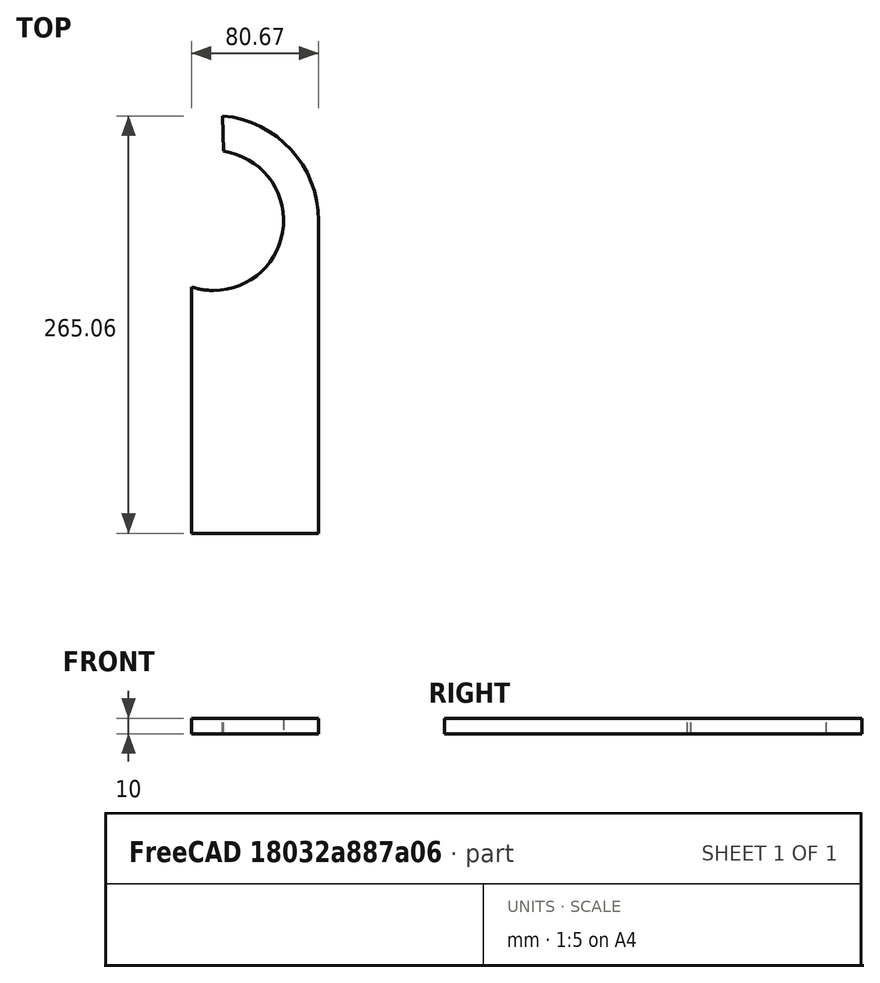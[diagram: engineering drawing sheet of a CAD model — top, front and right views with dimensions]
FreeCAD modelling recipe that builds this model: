
FCSTD DOCUMENT  (FreeCAD 0.21R33675 (Git))
Label: Tail_Stop_LowEnd
License: All rights reserved
LicenseURL: http://en.wikipedia.org/wiki/All_rights_reserved
objects: Sketcher::SketchObject×1, PartDesign::Pad×1, Spreadsheet::Sheet×1, PartDesign::Body×1
note: 4 computed .brp shape members not serialized (recipe doc carries the construction recipe); baked Part::Feature solids carry a one-line shape summary decoded from their .brp
EXTERNAL_REF file=../../Master_of_Puppets.FCStd obj=LowEndStop
EXTERNAL_REF file=../../Master_of_Puppets.FCStd obj=Spreadsheet
EXTERNAL_REF file=../../Master_of_Puppets.FCStd obj=Tail

FEATURE [Sketcher::SketchObject] Sketch
  FullyConstrained = true
  MapMode = 5
  Support = -> [XY_Plane001]
  expr: Constraints[13] = Spreadsheet.InnerArcAngle
  expr: Constraints[14] = Spreadsheet.OuterArcAngle
  expr: Constraints[15] = Spreadsheet.LowEndStopWidth
  expr: Constraints[1] = Spreadsheet.LowEndStopLength
  expr: Constraints[24] = Spreadsheet.LowEndStopWidth
  expr: Constraints[25] = Spreadsheet.LowEndStopLength
  expr: Constraints[33] = Spreadsheet.LowEndStopYawBearingOverlap
  expr: Constraints[7] = Spreadsheet.HingeOuterPipeRadius
  sketch-geometry (12):
    g0: LineSegment StartX=0 StartY=0 StartZ=0 EndX=0 EndY=-198.64 EndZ=0
    g1: LineSegment StartX=66.675 StartY=-198.64 StartZ=0 EndX=66.675 EndY=0 EndZ=0
    g2: ArcOfCircle CenterX=0 CenterY=0 CenterZ=0 NormalX=0 NormalY=0 NormalZ=1 AngleXU=0 Radius=66.675 StartAngle=0 EndAngle=1.48304
    g3: Circle CenterX=0 CenterY=0 CenterZ=0 NormalX=0 NormalY=0 NormalZ=1 AngleXU=0 Radius=44.45
    g4: ArcOfCircle CenterX=0 CenterY=0 CenterZ=0 NormalX=0 NormalY=0 NormalZ=1 AngleXU=0 Radius=44.45 StartAngle=4.71239 EndAngle=7.71269
    g5: LineSegment StartX=6.25936 StartY=44.0071 StartZ=0 EndX=5.84395 EndY=66.4184 EndZ=0
    g6: LineSegment StartX=-8.2e-15 StartY=-198.64 StartZ=0 EndX=-8.2e-15 EndY=-44.45 EndZ=0
    g7: ArcOfCircle CenterX=0 CenterY=0 CenterZ=0 NormalX=0 NormalY=0 NormalZ=1 AngleXU=0 Radius=44.45 StartAngle=4.71239 EndAngle=10.9956
    g8: LineSegment StartX=-8.2e-15 StartY=-198.64 StartZ=0 EndX=66.675 EndY=-198.64 EndZ=0
    g9: LineSegment StartX=-8.2e-15 StartY=-198.64 StartZ=0 EndX=-14 EndY=-198.64 EndZ=0
    g10: LineSegment StartX=-14 StartY=-198.64 StartZ=0 EndX=-14 EndY=-42.1877 EndZ=0
    g11: ArcOfCircle CenterX=0 CenterY=0 CenterZ=0 NormalX=0 NormalY=0 NormalZ=1 AngleXU=0 Radius=44.45 StartAngle=4.39197 EndAngle=4.71239
  constraints (34):
    c: Vertical(g1)
    c: Distance(g0) = 198.64
    c: Coincident(g0,g-1)
    c: Coincident(g2,g0)
    c: Coincident(g2,g1)
    c: PointOnObject(g1,g-1)
    c: Coincident(g3,g2)
    c: Radius(g3) = 44.45
    c: PointOnObject(g4,g0)
    c: Coincident(g4,g2)
    c: PointOnObject(g4,g3)
    c: Coincident(g5,g4)
    c: Coincident(g5,g2)
    c: Angle(g4) = 3.00031
    c: Angle(g2) = 1.48304
    c: DistanceX(g-2,g1) = 66.675
    c: Vertical(g6)
    c: Vertical(g0)
    c: Coincident(g7,g2)
    c: Coincident(g7,g4)
    c: Coincident(g7,g6)
    c: Coincident(g8,g6)
    c: Coincident(g8,g1)
    c: Horizontal(g8)
    c: DistanceX(g8,g8) = 66.675
    c: DistanceY(g6,g2) = 198.64
    c: Coincident(g9,g6)
    c: Horizontal(g9)
    c: Coincident(g10,g9)
    c: Vertical(g10)
    c: Coincident(g11,g2)
    c: Coincident(g11,g4)
    c: Coincident(g11,g10)
    c: DistanceX(g9,g9) = 14
FEATURE [PartDesign::Pad] Pad
  AllowMultiFace = false
  Direction = (0,0,1)
  Length = 10
  Length2 = 100
  Profile = -> Sketch
  Type = 0
  expr: Length = Spreadsheet.FlatMetalThickness
FEATURE [Spreadsheet::Sheet] Spreadsheet
  cells = A1='Inputs; A2='YawPipeDiameter; B2(YawPipeDiameter)==Master_of_Puppets#Spreadsheet.YawPipeDiameter; A3='FlatMetalThickness; B3(FlatMetalThickness)==Master_of_Puppets#Spreadsheet.FlatMetalThickness; A4='TailHingeJunctionFullWidth; B4(TailHingeJunctionFullWidth)==Master_of_Puppets#Tail.TailHingeJunctionFullWidth; A5='OuterTailHingeLowEndStopAngle; B5(OuterTailHingeLowEndStopAngle)==Master_of_Puppets#LowEndStop.LowEndStopAngle; A6='TailBoomTriangularBraceWidth; B6(TailBoomTriangularBraceWidth)==Master_of_Puppets#Tail.TailBoomTriangularBraceWidth; A7='TailAngle; B7(TailAngle)==Master_of_Puppets#Tail.TailAngle; A8='TailY; B8(TailBoomY)==Master_of_Puppets#Tail.TailY; A9='LowEndStopLength; B9(LowEndStopLength)==Master_of_Puppets#LowEndStop.LowEndStopLength; A10='RotorDiskRadius; B10(RotorDiskRadius)==Master_of_Puppets#Spreadsheet.RotorDiskRadius; A11='OuterLowEndStopWidth; B11(OuterLowEndStopWidth)==Master_of_Puppets#LowEndStop.OuterLowEndStopWidth; A12='LowEndStopYawBearingOverlap; B12(LowEndStopYawBearingOverlap)==Master_of_Puppets#LowEndStop.LowEndStopYawBearingOverlap; A13='LowEndStopWidth; B13(LowEndStopWidth)==Master_of_Puppets#LowEndStop.LowEndStopWidth; A14='HingeOuterPipeRadius; B14(HingeOuterPipeRadius)==Master_of_Puppets#Tail.HingeOuterPipeRadius; A15='Calculated; A16='HalfTriangularBraceThickness; B16(HalfTriangularBraceThickness)==FlatMetalThickness / 2; A17='TriangularBraceOffsetFactor; B17(TriangularBraceOffsetFactor)=-1; C17='Set TriangularBraceOffsetFactor to 1 to extend low end stop underneath boom & above boom support; A18='Inner Arc Angle; C18='Outer Arc Angle; A19='InnerTriangularBraceAngleOffset; B19(InnerTriangularBraceAngleOffset)==HalfTriangularBraceThickness / HingeOuterPipeRadius * 180 / pi * 1 deg * TriangularBraceOffsetFactor; C19='OuterTriangularBraceAngleOffset; D19(OuterTriangularBraceAngleOffset)==HalfTriangularBraceThickness / LowEndStopWidth * 180 / pi * 1 deg * TriangularBraceOffsetFactor; A20='InnerTailBoomYAngleOffset; B20(InnerTailBoomYAngleOffset)==TailBoomY / HingeOuterPipeRadius * 180 / pi * 1 deg; C20='OuterTailBoomYAngleOffset; D20(OuterTailBoomYAngleOffset)==TailBoomY / LowEndStopWidth * 180 / pi * 1 deg; C21='TailBoomRotationYOffset; D21(TailBoomRotationYOffset)==sin(TailAngle) * OuterLowEndStopWidth; A22='InnerAngle; B22(InnerAngle)==OuterTailHingeLowEndStopAngle + InnerTriangularBraceAngleOffset + InnerTailBoomYAngleOffset; C22='TailBoomRotationAngleOffset; D22(TailBoomRotationAngleOffset)==TailBoomRotationYOffset / LowEndStopWidth * 180 / pi * 1 deg; A23='InnerArcAngle; B23(InnerArcAngle)==90 deg + InnerAngle; C23='OuterArcAngle; D23(OuterArcAngle)==OuterTailHingeLowEndStopAngle + OuterTriangularBraceAngleOffset + OuterTailBoomYAngleOffset + TailBoomRotationAngleOffset
FEATURE [PartDesign::Body] PocketBody  label="Tail_Stop_LowEnd"
  Group = -> [Sketch,Pad]
  Origin = -> Origin001
  Tip = -> Pad
